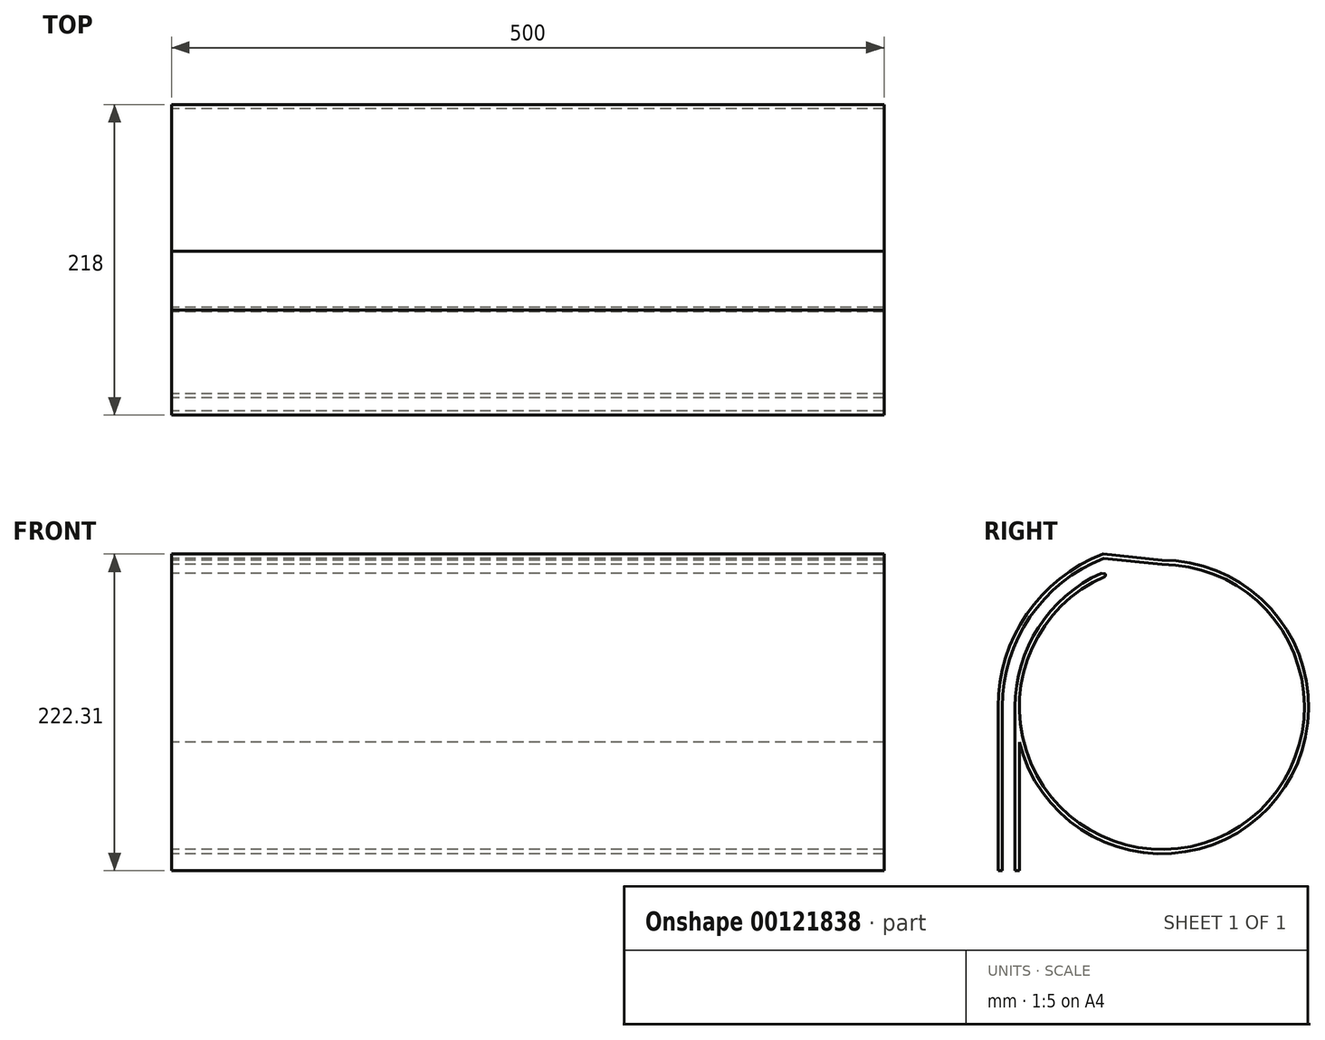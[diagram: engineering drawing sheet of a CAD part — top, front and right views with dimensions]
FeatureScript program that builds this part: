
annotation { "Feature Type Name" : "Feature", "Feature Type Description" : "" }
export const myFeature = defineFeature(function(context is Context, id is Id, definition is map)
    precondition{}
    {
        {
            var Q0;
            Q0=qCreatedBy(makeId("Right.planeOp"),FACE);
            var sketch = newSketch(context, id + "F0", { "sketchPlane" : qUnion([Q0])});
            skArc(sketch, "E0", {"start": v(-40.04, 91.63) * mm, "mid": v(20.45, -97.89) * mm, "end": v(0, 100) * mm});
            skLineSegment(sketch, "E1.bottom", {"start": v(115, -115) * mm, "end": v(-115, -115) * mm});
            skLineSegment(sketch, "E1.top", {"start": v(115, 115) * mm, "end": v(-115, 115) * mm});
            skLineSegment(sketch, "E1.left", {"start": v(115, -115) * mm, "end": v(115, 115) * mm});
            skLineSegment(sketch, "E1.right", {"start": v(-115, -115) * mm, "end": v(-115, 115) * mm});
            skArc(sketch, "E2", {"start": v(-42.6, 93.78) * mm, "mid": v(-86.6, 55.77) * mm, "end": v(-103, 0) * mm});
            skLineSegment(sketch, "E3", {"start": v(-100, 0) * mm, "end": v(-100, -115) * mm});
            skLineSegment(sketch, "E4", {"start": v(-103, 0) * mm, "end": v(-103, -115) * mm});
            skLineSegment(sketch, "E5", {"start": v(-112, 0) * mm, "end": v(-112, -115) * mm});
            skLineSegment(sketch, "E6", {"start": v(0, 103) * mm, "end": v(-41.34, 107.31) * mm});
            skLineSegment(sketch, "E7", {"start": v(0, 100) * mm, "end": v(-40.9, 104.27) * mm});
            skLineSegment(sketch, "E8", {"start": v(-42.6, 93.78) * mm, "end": v(-40.34, 93.54) * mm});
            skArc(sketch, "E9.trimOffspring", {"start": v(-100, -24.68) * mm, "mid": v(81.09, -63.51) * mm, "end": v(0, 103) * mm});
            skArc(sketch, "E10.trimOffspring", {"start": v(-41.34, 107.31) * mm, "mid": v(-94.81, 65.08) * mm, "end": v(-115, 0) * mm});
            skArc(sketch, "E11.trimOffspring", {"start": v(-40.9, 104.27) * mm, "mid": v(-92.53, 63.1) * mm, "end": v(-112, 0) * mm});
            skLineSegment(sketch, "E12", {"start": v(0, 103) * mm, "end": v(0, 100) * mm});
            skLineSegment(sketch, "E13", {"start": v(-41.34, 107.31) * mm, "end": v(-40.9, 104.27) * mm});
            skPoint(sketch, "E14.visualSharp", {"position": v(-36.42, 93.13) * mm});
            skArc(sketch, "E14.filletArc", {"start": v(-40.04, 91.63) * mm, "mid": v(-39.46, 92.7) * mm, "end": v(-40.34, 93.54) * mm});
            skSolve(sketch);
        }
        {
            var Q0;
            {var subQ0=sQuery(id+"F0.wireOp",EDGE,"E5");Q0=makeQuery(id+"F0.imprint","IMPRINT",FACE,{"disambiguationData":[TD([[makeQuery(id+"F0.imprint","IMPRINT",EDGE,{"derivedFrom":subQ0}),-1.0]])]});}
            var Q1;
            Q1=makeQuery(id+"F0.imprint","IMPRINT",FACE,{"disambiguationData":[TD([[makeQuery(id+"F0.imprint","IMPRINT",EDGE,{"derivedFrom":sQuery(id+"F0.wireOp",EDGE,"E2")}),1.0]])]});
            var Q2;
            {var subQ4=sQuery(id+"F0.wireOp",EDGE,"E9.trimOffspring");Q2=makeQuery(id+"F0.imprint","IMPRINT",FACE,{"disambiguationData":[TD([[makeQuery(id+"F0.imprint","IMPRINT",EDGE,{"derivedFrom":subQ4}),1.0]])]});}
            var Q3;
            Q3=makeQuery(id+"F0.imprint","IMPRINT",FACE,{"disambiguationData":[TD([[makeQuery(id+"F0.imprint","IMPRINT",EDGE,{"derivedFrom":sQuery(id+"F0.wireOp",EDGE,"E6")}),1.0]])]});
            extrude(context, id + "F1", {"entities" : qUnion([Q0, Q1, Q2, Q3]), "depth" : (500) * mm});
        }
    });
